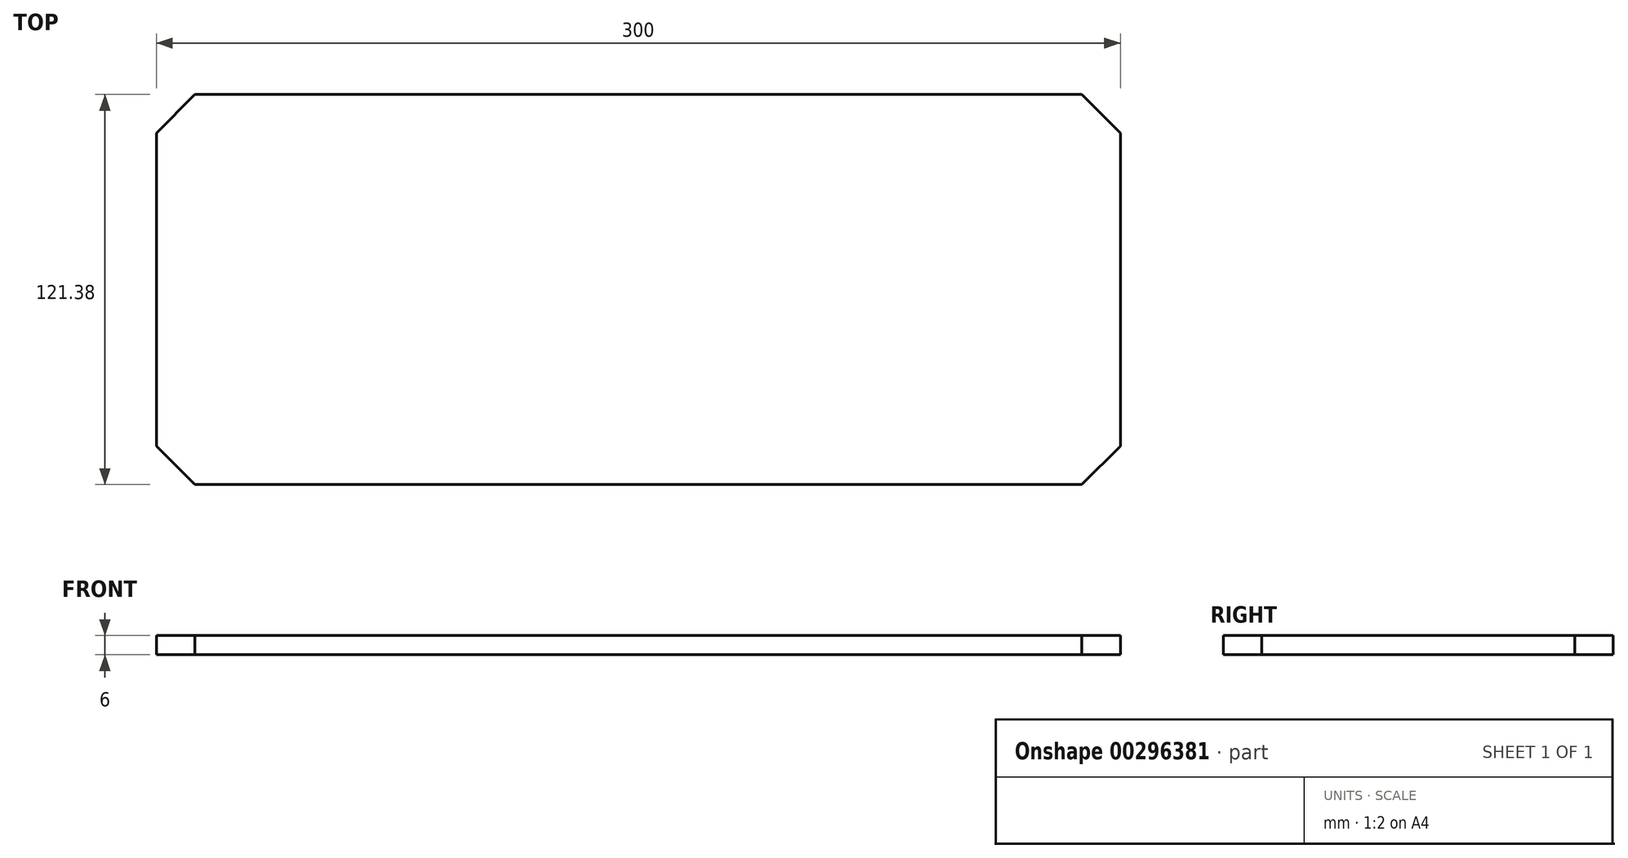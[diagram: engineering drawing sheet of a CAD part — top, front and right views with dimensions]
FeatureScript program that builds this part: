
annotation { "Feature Type Name" : "Feature", "Feature Type Description" : "" }
export const myFeature = defineFeature(function(context is Context, id is Id, definition is map)
    precondition{}
    {
        {
            var Q0;
            Q0=qCreatedBy(makeId("Top.planeOp"),FACE);
            var sketch = newSketch(context, id + "F0", { "sketchPlane" : qUnion([Q0])});
            skLineSegment(sketch, "E0.bottom", {"start": v(-154.19, 68.14) * mm, "end": v(145.81, 68.14) * mm});
            skLineSegment(sketch, "E0.top", {"start": v(-154.19, -53.24) * mm, "end": v(145.81, -53.24) * mm});
            skLineSegment(sketch, "E0.left", {"start": v(-154.19, 68.14) * mm, "end": v(-154.19, -53.24) * mm});
            skLineSegment(sketch, "E0.right", {"start": v(145.81, 68.14) * mm, "end": v(145.81, -53.24) * mm});
            skSolve(sketch);
        }
        {
            var Q0;
            Q0=makeQuery(id+"F0.imprint","IMPRINT",FACE,{"disambiguationData":[TD([[makeQuery(id+"F0.imprint","IMPRINT",EDGE,{"derivedFrom":sQuery(id+"F0.wireOp",EDGE,"E0.bottom")}),-1.0]])]});
            extrude(context, id + "F1", {"entities" : qUnion([Q0]), "depth" : 6 * mm});
        }
        {
            var Q0;
            Q0=makeQuery(id+"F1.opExtrude","SWEPT_EDGE",EDGE,{"disambiguationData":[OSD([sQuery(id+"F0.wireOp",EDGE,"E0.bottom"),sQuery(id+"F0.wireOp",EDGE,"E0.right")])]});
            var Q1;
            Q1=makeQuery(id+"F1.opExtrude","SWEPT_EDGE",EDGE,{"disambiguationData":[OSD([sQuery(id+"F0.wireOp",EDGE,"E0.bottom"),sQuery(id+"F0.wireOp",EDGE,"E0.left")])]});
            var Q2;
            Q2=makeQuery(id+"F1.opExtrude","SWEPT_EDGE",EDGE,{"disambiguationData":[OSD([sQuery(id+"F0.wireOp",EDGE,"E0.top"),sQuery(id+"F0.wireOp",EDGE,"E0.left")])]});
            var Q3;
            Q3=makeQuery(id+"F1.opExtrude","SWEPT_EDGE",EDGE,{"disambiguationData":[OSD([sQuery(id+"F0.wireOp",EDGE,"E0.top"),sQuery(id+"F0.wireOp",EDGE,"E0.right")])]});
            chamfer(context, id + "F2", {"entities" : qUnion([Q0, Q1, Q2, Q3]), "width" : 12 * mm, "tangentPropagation" : true});
        }
    });
